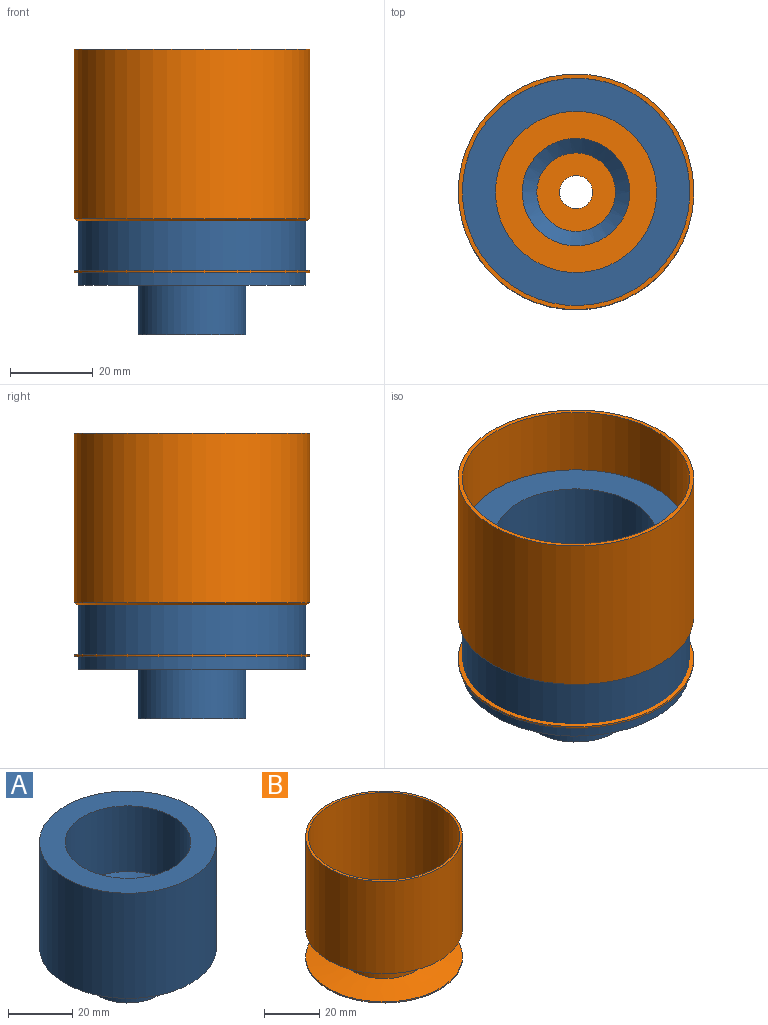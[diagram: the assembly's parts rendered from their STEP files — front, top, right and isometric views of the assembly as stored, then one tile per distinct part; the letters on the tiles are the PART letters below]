
ASSEMBLY  parts=2 mates=1
PART A: 10 faces, bbox 55x55x52 mm
  f0: plane 55x55mm, normal (0,0,1), area 1181.2mm2, adj f1,f9
  f1: cylinder r=19.5mm len=39mm, axis (0,0,-1), area 3063.1mm2, adj f0,f2
  f2: cone r=19.5mm half-angle=55deg, axis (0,0,1), area 1112.1mm2, adj f1,f3
  f3: cylinder r=9.5mm len=19mm, axis (0,0,-1), area 238.8mm2, adj f2,f4
  f4: plane 19x19mm, normal (0,0,1), area 82.5mm2, adj f3,f5
  f5: cylinder r=8mm len=16mm, axis (0,0,-1), area 804.2mm2, adj f4,f6
  f6: plane 26x26mm, normal (0,0,-1), area 329.9mm2, adj f5,f7
  f7: cylinder r=13mm len=26mm, axis (0,0,-1), area 980.2mm2, adj f6,f8
  f8: plane 55x55mm, normal (0,0,-1), area 1844.9mm2, adj f7,f9
  f9: cylinder r=27.5mm len=55mm, axis (0,0,-1), area 6911.5mm2, adj f0,f8
PART B: 12 faces, bbox 57x57x54 mm
  f0: plane 55x55mm, normal (0,0,1), area 1844.9mm2, adj f1,f11
  f1: cylinder r=13mm len=26mm, axis (0,0,1), area 980.2mm2, adj f0,f2
  f2: plane 26x26mm, normal (0,0,1), area 480.7mm2, adj f1,f3
  f3: cylinder r=4mm len=8mm, axis (0,0,1), area 50.3mm2, adj f2,f4
  f4: plane 57x57mm, normal (0,0,-1), area 2501.5mm2, adj f3,f5
  f5: cylinder r=28.5mm len=57mm, axis (0,0,1), area 89.5mm2, adj f4,f6
  f6: cone r=16mm half-angle=83.2deg, axis (0,0,-1), area 1760mm2, adj f5,f7
  f7: cylinder r=16mm len=32mm, axis (0,0,1), area 380.3mm2, adj f6,f8
  f8: cone r=16mm half-angle=60deg, axis (0,0,1), area 2017.9mm2, adj f7,f9
  f9: cylinder r=28.5mm len=57mm, axis (0,0,1), area 7341.9mm2, adj f8,f10
  f10: plane 57x57mm, normal (0,0,1), area 175.9mm2, adj f9,f11
  f11: cylinder r=27.5mm len=55mm, axis (0,0,1), area 6911.5mm2, adj f0,f10
PLACE A t=(-11,4.59,2.41)mm
PLACE B rot(axis=(0,0,1),180deg) t=(-11,4.59,19.41)mm
MATE slider B.f1 <-> A.f1  axis (0,0,1) through (-11,4.59,7.41)mm
